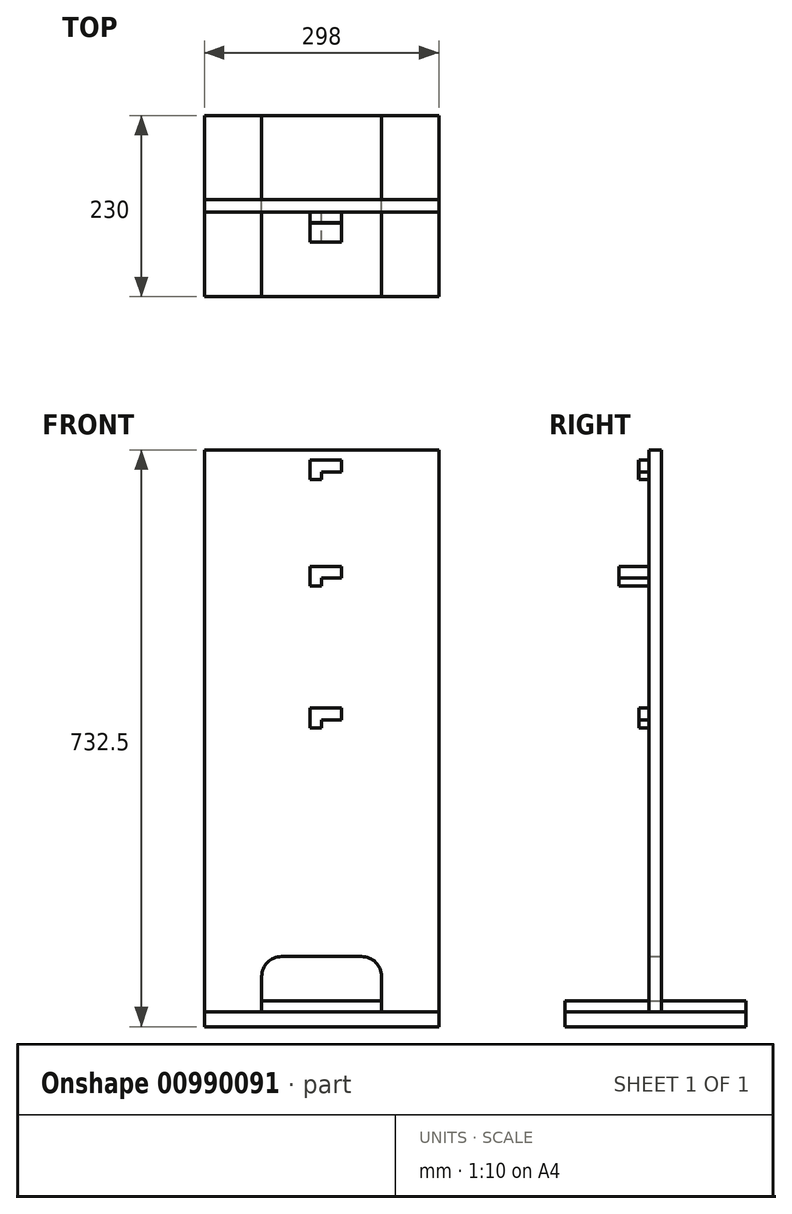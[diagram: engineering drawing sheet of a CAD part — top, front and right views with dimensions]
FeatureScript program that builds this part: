
annotation { "Feature Type Name" : "Feature", "Feature Type Description" : "" }
export const myFeature = defineFeature(function(context is Context, id is Id, definition is map)
    precondition{}
    {
        {
            var Q0;
            Q0=qCreatedBy(makeId("Front.planeOp"),FACE);
            var sketch = newSketch(context, id + "F0", { "sketchPlane" : qUnion([Q0])});
            skLineSegment(sketch, "E0.bottom", {"start": v(76, 0) * mm, "end": v(-76, 0) * mm});
            skLineSegment(sketch, "E0.top", {"start": v(76, -13.5) * mm, "end": v(-76, -13.5) * mm});
            skLineSegment(sketch, "E0.left", {"start": v(76, 0) * mm, "end": v(76, -13.5) * mm});
            skLineSegment(sketch, "E0.right", {"start": v(-76, 0) * mm, "end": v(-76, -13.5) * mm});
            skLineSegment(sketch, "E1", {"start": v(0, 672.3) * mm, "end": v(0, 0) * mm, "construction": true});
            skLineSegment(sketch, "E2.bottom", {"start": v(-149, -13.5) * mm, "end": v(149, -13.5) * mm});
            skLineSegment(sketch, "E2.top", {"start": v(-149, -32.5) * mm, "end": v(149, -32.5) * mm});
            skLineSegment(sketch, "E2.left", {"start": v(-149, -13.5) * mm, "end": v(-149, -32.5) * mm});
            skLineSegment(sketch, "E2.right", {"start": v(149, -13.5) * mm, "end": v(149, -32.5) * mm});
            skPoint(sketch, "E2.middle", {"position": v(0, -23) * mm});
            skLineSegment(sketch, "E3", {"start": v(-149, -13.5) * mm, "end": v(-149, 700) * mm});
            skLineSegment(sketch, "E4", {"start": v(-149, 700) * mm, "end": v(149, 700) * mm});
            skLineSegment(sketch, "E5", {"start": v(149, 700) * mm, "end": v(149, -13.5) * mm});
            skLineSegment(sketch, "E6", {"start": v(-76, 0) * mm, "end": v(-76, 31.5) * mm});
            skLineSegment(sketch, "E7", {"start": v(-51, 56.5) * mm, "end": v(51, 56.5) * mm});
            skLineSegment(sketch, "E8", {"start": v(76, 31.5) * mm, "end": v(76, -13.5) * mm});
            skPoint(sketch, "E9.visualSharp", {"position": v(76, 56.5) * mm});
            skArc(sketch, "E9.filletArc", {"start": v(76, 31.5) * mm, "mid": v(68.68, 49.18) * mm, "end": v(51, 56.5) * mm});
            skPoint(sketch, "E10.visualSharp", {"position": v(-76, 56.5) * mm});
            skArc(sketch, "E10.filletArc", {"start": v(-51, 56.5) * mm, "mid": v(-68.68, 49.18) * mm, "end": v(-76, 31.5) * mm});
            skLineSegment(sketch, "E11", {"start": v(0, 672.3) * mm, "end": v(0, 662.3) * mm});
            skLineSegment(sketch, "E12", {"start": v(0, 662.3) * mm, "end": v(-15, 662.3) * mm});
            skLineSegment(sketch, "E13", {"start": v(-15, 662.3) * mm, "end": v(-15, 687.3) * mm});
            skLineSegment(sketch, "E14", {"start": v(-15, 687.3) * mm, "end": v(25, 687.3) * mm});
            skLineSegment(sketch, "E15", {"start": v(25, 687.3) * mm, "end": v(25, 672.3) * mm});
            skLineSegment(sketch, "E16", {"start": v(-25.6, 1342.78) * mm, "end": v(-25.6, 1367.78) * mm});
            skLineSegment(sketch, "E17", {"start": v(0, 537.3) * mm, "end": v(0, 527.3) * mm});
            skLineSegment(sketch, "E18", {"start": v(0, 527.3) * mm, "end": v(-15, 527.3) * mm});
            skLineSegment(sketch, "E19", {"start": v(-15, 527.3) * mm, "end": v(-15, 552.3) * mm});
            skLineSegment(sketch, "E20", {"start": v(-15, 552.3) * mm, "end": v(25, 552.3) * mm});
            skLineSegment(sketch, "E21", {"start": v(25, 552.3) * mm, "end": v(25, 537.3) * mm});
            skLineSegment(sketch, "E22", {"start": v(0, 357.3) * mm, "end": v(0, 347.3) * mm});
            skLineSegment(sketch, "E23", {"start": v(0, 347.3) * mm, "end": v(-15, 347.3) * mm});
            skLineSegment(sketch, "E24", {"start": v(-15, 347.3) * mm, "end": v(-15, 372.3) * mm});
            skLineSegment(sketch, "E25", {"start": v(-15, 372.3) * mm, "end": v(25, 372.3) * mm});
            skLineSegment(sketch, "E26", {"start": v(25, 372.3) * mm, "end": v(25, 357.3) * mm});
            skPoint(sketch, "E27", {"position": v(113, 100) * mm});
            skPoint(sketch, "E28", {"position": v(134, 200) * mm});
            skPoint(sketch, "E29", {"position": v(93, 400) * mm});
            skFitSpline(sketch, "E30", {"points": [v(0, 672.3) * mm, v(93, 400) * mm, v(134, 200) * mm, v(113, 100) * mm, v(51, 31.5) * mm, v(0, 0) * mm], "startDerivative": vector(303.44, -949.91) * mm, "endDerivative": vector(-376.27, -202.89) * mm});
            skLineSegment(sketch, "E31", {"start": v(0, 672.3) * mm, "end": v(25, 672.3) * mm});
            skLineSegment(sketch, "E32", {"start": v(0, 537.3) * mm, "end": v(25, 537.3) * mm});
            skLineSegment(sketch, "E33", {"start": v(0, 357.3) * mm, "end": v(25, 357.3) * mm});
            skSolve(sketch);
        }
        {
            var Q0;
            Q0=makeQuery(id+"F0.imprint","IMPRINT",FACE,{"disambiguationData":[TD([[makeQuery(id+"F0.imprint","IMPRINT",EDGE,{"derivedFrom":sQuery(id+"F0.wireOp",EDGE,"E0.bottom")}),1.0]])]});
            extrude(context, id + "F1", {"entities" : qUnion([Q0]), "depth" : 115 * mm, "offsetDistance" : 25 * mm, "hasSecondDirection" : true, "secondDirectionOppositeDirection" : true, "secondDirectionDepth" : 115 * mm});
        }
        {
            var Q0;
            Q0=makeQuery(id+"F0.imprint","IMPRINT",FACE,{"disambiguationData":[TD([[makeQuery(id+"F0.imprint","IMPRINT",EDGE,{"derivedFrom":sQuery(id+"F0.wireOp",EDGE,"E2.top")}),1.0]])]});
            extrude(context, id + "F2", {"entities" : qUnion([Q0]), "depth" : 115 * mm, "offsetDistance" : 25 * mm, "hasSecondDirection" : true, "secondDirectionOppositeDirection" : true, "secondDirectionDepth" : 115 * mm});
        }
        {
            var Q0;
            {var subQ5=sQuery(id+"F0.wireOp",EDGE,"E0.right");Q0=makeQuery(id+"F0.imprint","IMPRINT",FACE,{"disambiguationData":[TD([[makeQuery(id+"F0.imprint","IMPRINT",EDGE,{"derivedFrom":subQ5}),-1.0]])]});}
            extrude(context, id + "F3", {"entities" : qUnion([Q0]), "depth" : 8 * mm, "offsetDistance" : 25 * mm, "hasSecondDirection" : true, "secondDirectionOppositeDirection" : true, "secondDirectionDepth" : 8 * mm});
        }
        {
            var Q0;
            Q0=makeQuery(id+"F0.imprint","IMPRINT",FACE,{"disambiguationData":[TD([[makeQuery(id+"F0.imprint","IMPRINT",EDGE,{"derivedFrom":sQuery(id+"F0.wireOp",EDGE,"E11")}),-1.0]])]});
            extrude(context, id + "F4", {"entities" : qUnion([Q0]), "operationType" : NewBodyOperationType.ADD, "depth" : 21 * mm, "offsetDistance" : 25 * mm, "hasSecondDirection" : true, "secondDirectionOppositeDirection" : true, "secondDirectionDepth" : 8 * mm});
        }
        {
            var Q0;
            Q0=makeQuery(id+"F0.imprint","IMPRINT",FACE,{"disambiguationData":[TD([[makeQuery(id+"F0.imprint","IMPRINT",EDGE,{"derivedFrom":sQuery(id+"F0.wireOp",EDGE,"E17")}),-1.0]])]});
            extrude(context, id + "F5", {"entities" : qUnion([Q0]), "operationType" : NewBodyOperationType.ADD, "depth" : 21 * mm, "offsetDistance" : 25 * mm, "hasSecondDirection" : true, "secondDirectionOppositeDirection" : true, "secondDirectionDepth" : 8 * mm});
        }
        {
            var Q0;
            Q0=makeQuery(id+"F0.imprint","IMPRINT",FACE,{"disambiguationData":[TD([[makeQuery(id+"F0.imprint","IMPRINT",EDGE,{"derivedFrom":sQuery(id+"F0.wireOp",EDGE,"E22")}),-1.0]])]});
            extrude(context, id + "F6", {"entities" : qUnion([Q0]), "operationType" : NewBodyOperationType.ADD, "depth" : 21 * mm, "offsetDistance" : 25 * mm, "hasSecondDirection" : true, "secondDirectionOppositeDirection" : true, "secondDirectionDepth" : 8 * mm});
        }
        {
            var Q0;
            Q0=makeQuery(id+"F4.opExtrude","CAP_FACE",FACE,{"disambiguationData":[OSD([sQuery(id+"F0.wireOp",EDGE,"E11"),sQuery(id+"F0.wireOp",EDGE,"E12"),sQuery(id+"F0.wireOp",EDGE,"E13"),sQuery(id+"F0.wireOp",EDGE,"E14"),sQuery(id+"F0.wireOp",EDGE,"E15"),sQuery(id+"F0.wireOp",EDGE,"E31")])],"isStart":false});
            cPlane(context, id + "F7", {"entities" : qUnion([Q0]), "cplaneType" : CPlaneType.OFFSET, "offset" : .2 * mm, "width" : 150 * mm, "height" : 150 * mm});
        }
        {
            var Q0;
            Q0=qCreatedBy(id+"F7.planeOp",FACE);
            var sketch = newSketch(context, id + "F8", { "sketchPlane" : qUnion([Q0])});
            skLineSegment(sketch, "E34", {"start": v(-15, 687.3) * mm, "end": v(25, 687.3) * mm});
            skLineSegment(sketch, "E35", {"start": v(25, 687.3) * mm, "end": v(25, 672.3) * mm});
            skLineSegment(sketch, "E36", {"start": v(25, 672.3) * mm, "end": v(0, 672.3) * mm});
            skLineSegment(sketch, "E37", {"start": v(0, 672.3) * mm, "end": v(0, 662.3) * mm});
            skLineSegment(sketch, "E38", {"start": v(0, 662.3) * mm, "end": v(-15, 662.3) * mm});
            skLineSegment(sketch, "E39", {"start": v(-15, 662.3) * mm, "end": v(-15, 687.3) * mm});
            skSolve(sketch);
        }
        {
            var Q0;
            Q0=makeQuery(id+"F8.imprint","IMPRINT",FACE,{"disambiguationData":[TD([[makeQuery(id+"F8.imprint","IMPRINT",EDGE,{"derivedFrom":sQuery(id+"F8.wireOp",EDGE,"E34")}),-1.0]])]});
            extrude(context, id + "F9", {"entities" : qUnion([Q0]), "depth" : .5 * mm, "offsetDistance" : 25 * mm});
        }
        {
            var Q0;
            Q0=qCreatedBy(id+"F7.planeOp",FACE);
            var sketch = newSketch(context, id + "F10", { "sketchPlane" : qUnion([Q0])});
            skLineSegment(sketch, "E40", {"start": v(0, 537.3) * mm, "end": v(0, 527.3) * mm});
            skLineSegment(sketch, "E41", {"start": v(0, 527.3) * mm, "end": v(-15, 527.3) * mm});
            skLineSegment(sketch, "E42", {"start": v(-15, 527.3) * mm, "end": v(-15, 552.3) * mm});
            skLineSegment(sketch, "E43", {"start": v(-15, 552.3) * mm, "end": v(25, 552.3) * mm});
            skLineSegment(sketch, "E44", {"start": v(25, 552.3) * mm, "end": v(25, 537.3) * mm});
            skSolve(sketch);
        }
        {
            var Q0;
            Q0=makeQuery(id+"F5.opExtrude","CAP_FACE",FACE,{"disambiguationData":[OSD([sQuery(id+"F0.wireOp",EDGE,"E17"),sQuery(id+"F0.wireOp",EDGE,"E18"),sQuery(id+"F0.wireOp",EDGE,"E19"),sQuery(id+"F0.wireOp",EDGE,"E20"),sQuery(id+"F0.wireOp",EDGE,"E21"),sQuery(id+"F0.wireOp",EDGE,"E32")])],"isStart":false});
            var Q1;
            Q1 = qSketchRegion(id + "F10", true);
            extrude(context, id + "F11", {"entities" : qUnion([Q0, Q1]), "operationType" : NewBodyOperationType.ADD, "depth" : 25 * mm, "offsetDistance" : 25 * mm});
        }
    });
